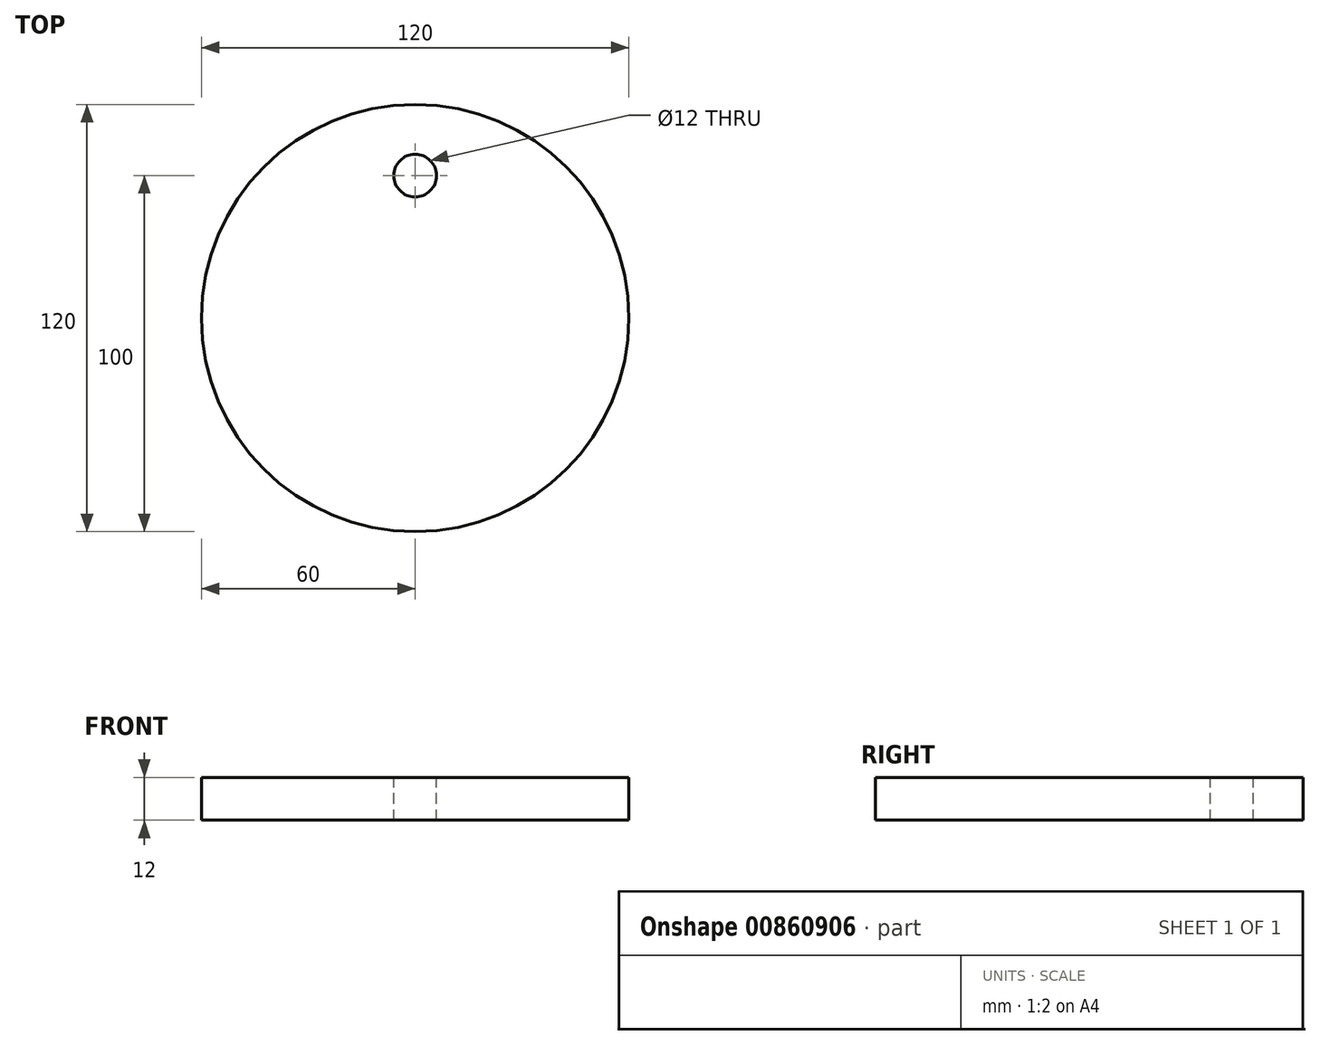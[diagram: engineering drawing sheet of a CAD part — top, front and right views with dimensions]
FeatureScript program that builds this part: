
annotation { "Feature Type Name" : "Feature", "Feature Type Description" : "" }
export const myFeature = defineFeature(function(context is Context, id is Id, definition is map)
    precondition{}
    {
        {
            assignVariable(context, id + "F0", {"name" : "bigcircle", "anyValue" : 120});
        }
        {
            assignVariable(context, id + "F1", {"name" : "thickness", "anyValue" : getVariable(context, 'bigcircle') / 10});
        }
        {
            var Q0;
            Q0=qCreatedBy(makeId("Top.planeOp"),FACE);
            var sketch = newSketch(context, id + "F2", { "sketchPlane" : qUnion([Q0])});
            skCircle(sketch, "E0", {"center": v(0, 0) * mm, "radius": 60 * mm});
            skSolve(sketch);
        }
        {
            var Q0;
            Q0=makeQuery(id+"F2.imprint","IMPRINT",FACE,{"disambiguationData":[TD([[makeQuery(id+"F2.imprint","IMPRINT",EDGE,{"derivedFrom":sQuery(id+"F2.wireOp",EDGE,"E0")}),1.0]])]});
            extrude(context, id + "F3", {"entities" : qUnion([Q0]), "depth" : (getVariable(context, 'thickness')) * mm, "offsetDistance" : 25 * mm});
        }
        {
            var Q0;
            Q0=makeQuery(id+"F3.opExtrude","CAP_FACE",FACE,{"disambiguationData":[OSD([sQuery(id+"F2.wireOp",EDGE,"E0")])],"isStart":false});
            var sketch = newSketch(context, id + "F4", { "sketchPlane" : qUnion([Q0])});
            skCircle(sketch, "E1", {"center": v(0, 0) * mm, "radius": 40 * mm, "construction": true});
            skCircle(sketch, "E2", {"center": v(0, 40) * mm, "radius": 6 * mm});
            skSolve(sketch);
        }
        {
            var Q0;
            Q0=makeQuery(id+"F4.imprint","IMPRINT",FACE,{"disambiguationData":[TD([[makeQuery(id+"F4.imprint","IMPRINT",EDGE,{"derivedFrom":sQuery(id+"F4.wireOp",EDGE,"E2")}),1.0]])]});
            var Q1;
            Q1=sQuery(id+"F4.wireOp",EDGE,"E2");
            extrude(context, id + "F5", {"entities" : qUnion([Q0]), "operationType" : NewBodyOperationType.REMOVE, "surfaceEntities" : qUnion([Q1]), "endBound" : BoundingType.THROUGH_ALL, "oppositeDirection" : true, "depth" : 25 * mm, "offsetDistance" : 25 * mm});
        }
    });
